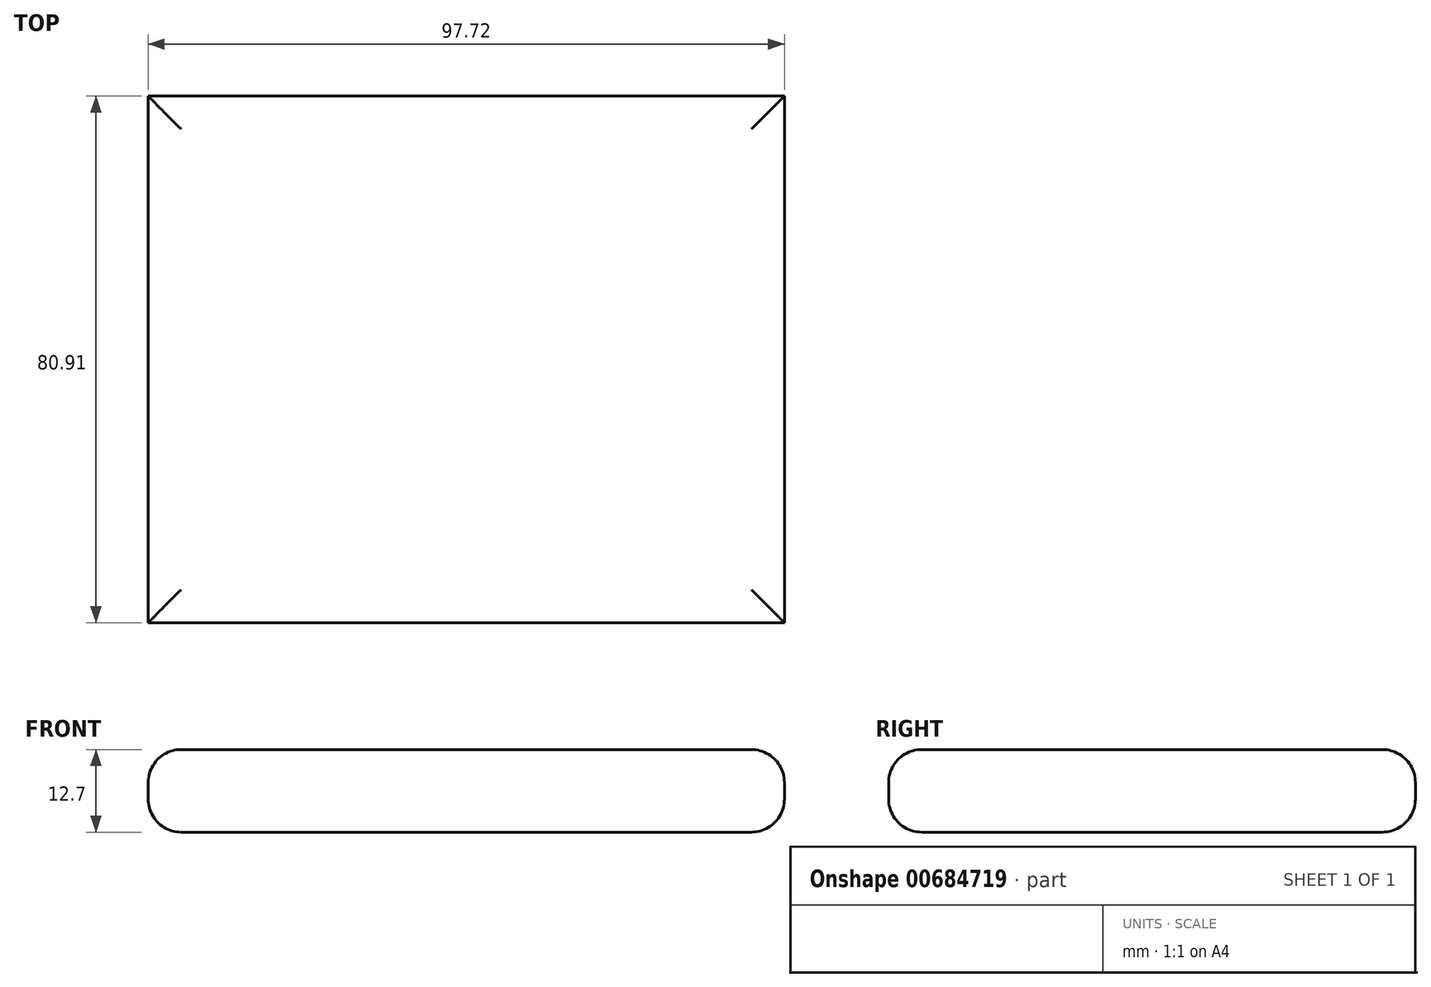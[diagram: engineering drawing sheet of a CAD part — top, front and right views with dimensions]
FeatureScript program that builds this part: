
annotation { "Feature Type Name" : "Feature", "Feature Type Description" : "" }
export const myFeature = defineFeature(function(context is Context, id is Id, definition is map)
    precondition{}
    {
        {
            var Q0;
            Q0=qCreatedBy(makeId("Top.planeOp"),FACE);
            var sketch = newSketch(context, id + "F0", { "sketchPlane" : qUnion([Q0])});
            skLineSegment(sketch, "E0.bottom", {"start": v(-48.55, 44.4) * mm, "end": v(49.17, 44.4) * mm});
            skLineSegment(sketch, "E0.top", {"start": v(-48.55, -36.51) * mm, "end": v(49.17, -36.51) * mm});
            skLineSegment(sketch, "E0.left", {"start": v(-48.55, 44.4) * mm, "end": v(-48.55, -36.51) * mm});
            skLineSegment(sketch, "E0.right", {"start": v(49.17, 44.4) * mm, "end": v(49.17, -36.51) * mm});
            skSolve(sketch);
        }
        {
            var Q0;
            Q0=makeQuery(id+"F0.imprint","IMPRINT",FACE,{"disambiguationData":[TD([[makeQuery(id+"F0.imprint","IMPRINT",EDGE,{"derivedFrom":sQuery(id+"F0.wireOp",EDGE,"E0.bottom")}),-1.0]])]});
            extrude(context, id + "F1", {"entities" : qUnion([Q0]), "depth" : 0 * mm, "offsetDistance" : 25.4 * mm, "hasSecondDirection" : true, "secondDirectionOppositeDirection" : true, "secondDirectionDepth" : 12.7 * mm});
        }
        {
            var Q0;
            Q0=makeQuery(id+"F1.opExtrude","CAP_FACE",FACE,{"disambiguationData":[OSD([sQuery(id+"F0.wireOp",EDGE,"E0.bottom"),sQuery(id+"F0.wireOp",EDGE,"E0.top"),sQuery(id+"F0.wireOp",EDGE,"E0.left"),sQuery(id+"F0.wireOp",EDGE,"E0.right")])],"isStart":false});
            var Q1;
            Q1=makeQuery(id+"F1.opExtrude","CAP_EDGE",EDGE,{"disambiguationData":[OSD([sQuery(id+"F0.wireOp",EDGE,"E0.top")])],"isStart":false});
            var Q2;
            Q2=makeQuery(id+"F1.opExtrude","CAP_EDGE",EDGE,{"disambiguationData":[OSD([sQuery(id+"F0.wireOp",EDGE,"E0.top")])],"isStart":true});
            var Q3;
            Q3=makeQuery(id+"F1.opExtrude","CAP_EDGE",EDGE,{"disambiguationData":[OSD([sQuery(id+"F0.wireOp",EDGE,"E0.right")])],"isStart":true});
            var Q4;
            Q4=makeQuery(id+"F1.opExtrude","CAP_EDGE",EDGE,{"disambiguationData":[OSD([sQuery(id+"F0.wireOp",EDGE,"E0.bottom")])],"isStart":true});
            var Q5;
            Q5=makeQuery(id+"F1.opExtrude","CAP_EDGE",EDGE,{"disambiguationData":[OSD([sQuery(id+"F0.wireOp",EDGE,"E0.left")])],"isStart":true});
            fillet(context, id + "F2", {"entities" : qUnion([Q0, Q1, Q2, Q3, Q4, Q5]), "radius" : 5.08 * mm, "tangentPropagation" : true, "allowEdgeOverflow" : false});
        }
    });
